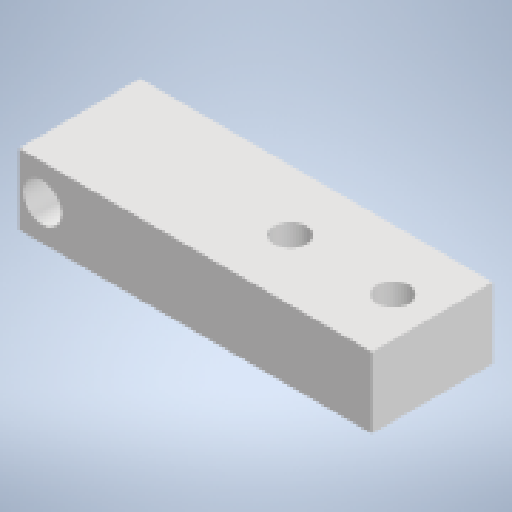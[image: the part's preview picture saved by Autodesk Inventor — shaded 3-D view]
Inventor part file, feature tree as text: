
AUTODESK INVENTOR PART (.ipt)
format: ipt  version: 2024.3 (Build 283343000, 343)  size: 128,000 bytes
history: native  units: mm
features: other x3, sketch x1
ambient origin geometry x8: Origin, YZ Plane, XZ Plane, XY Plane, X Axis, Y Axis, Z Axis, Center Point
bodies: Solid1 (feature_tree)
feature tree (4):
  other  "dedos.ipt"
  other  "Solid1::dedos.ipt"
  other  "TaggingFeature1"
  sketch  "Sketch1"  dims[d0=10.0mm]
